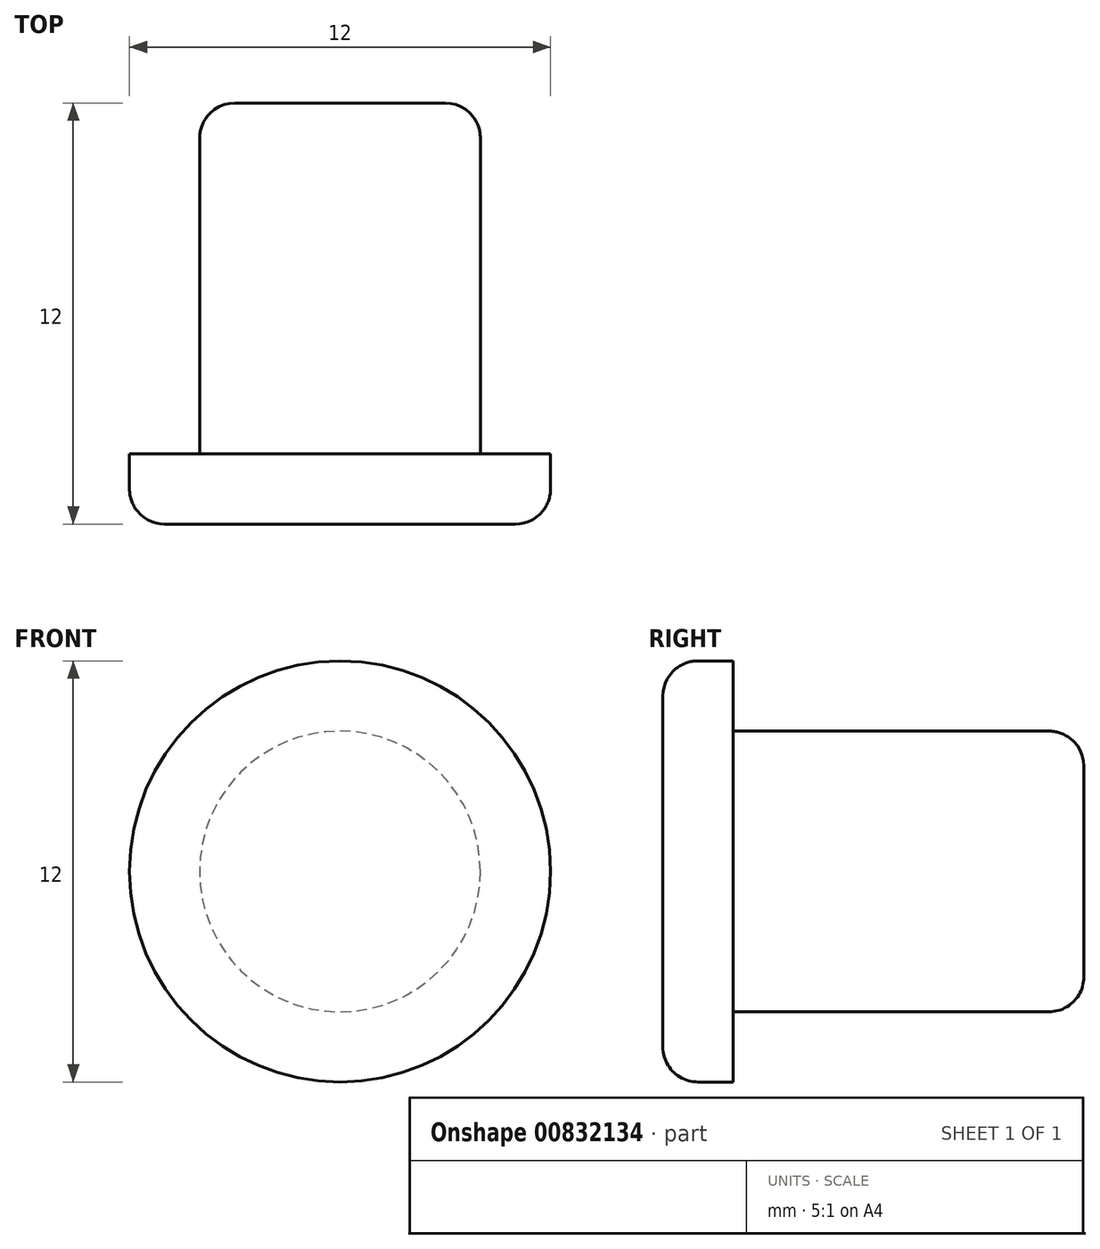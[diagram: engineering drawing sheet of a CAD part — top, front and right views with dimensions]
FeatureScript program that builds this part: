
annotation { "Feature Type Name" : "Feature", "Feature Type Description" : "" }
export const myFeature = defineFeature(function(context is Context, id is Id, definition is map)
    precondition{}
    {
        {
            var Q0;
            Q0=qCreatedBy(makeId("Front.planeOp"),FACE);
            var sketch = newSketch(context, id + "F0", { "sketchPlane" : qUnion([Q0])});
            skCircle(sketch, "E0", {"center": v(0, 0) * mm, "radius": 4 * mm});
            skSolve(sketch);
        }
        {
            var Q0;
            Q0 = qSketchRegion(id + "F0", true);
            extrude(context, id + "F1", {"entities" : qUnion([Q0]), "depth" : 10 * mm, "offsetDistance" : 25.4 * mm});
        }
        {
            var Q0;
            Q0=makeQuery(id+"F1.opExtrude","CAP_FACE",FACE,{"disambiguationData":[OSD([sQuery(id+"F0.wireOp",EDGE,"E0")])],"isStart":false});
            var sketch = newSketch(context, id + "F2", { "sketchPlane" : qUnion([Q0])});
            skCircle(sketch, "E1", {"center": v(0, 0) * mm, "radius": 6 * mm});
            skSolve(sketch);
        }
        {
            var Q0;
            Q0 = qSketchRegion(id + "F2", true);
            extrude(context, id + "F3", {"entities" : qUnion([Q0]), "operationType" : NewBodyOperationType.ADD, "depth" : 2 * mm, "offsetDistance" : 25.4 * mm});
        }
        {
            var Q0;
            Q0=makeQuery(id+"F1.opExtrude","CAP_EDGE",EDGE,{"disambiguationData":[OSD([sQuery(id+"F0.wireOp",EDGE,"E0")])],"isStart":true});
            var Q1;
            Q1=makeQuery(id+"F3.opExtrude","CAP_EDGE",EDGE,{"disambiguationData":[OSD([sQuery(id+"F2.wireOp",EDGE,"E1")])],"isStart":false});
            fillet(context, id + "F4", {"entities" : qUnion([Q0, Q1]), "radius" : 1 * mm, "tangentPropagation" : true, "allowEdgeOverflow" : false});
        }
    });
